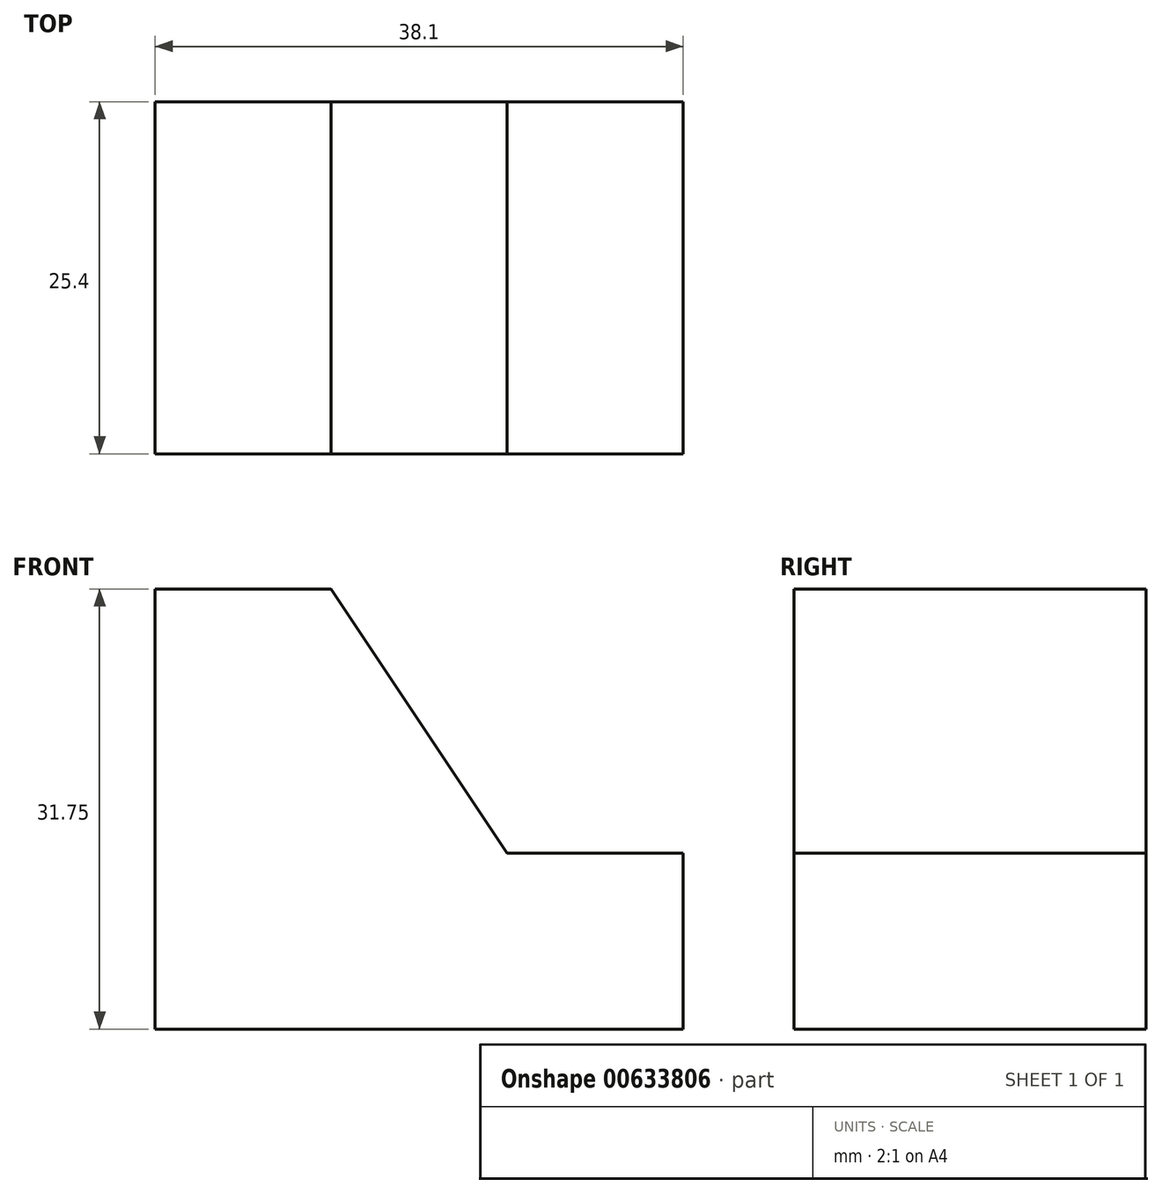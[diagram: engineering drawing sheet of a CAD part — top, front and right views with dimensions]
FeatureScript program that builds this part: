
annotation { "Feature Type Name" : "Feature", "Feature Type Description" : "" }
export const myFeature = defineFeature(function(context is Context, id is Id, definition is map)
    precondition{}
    {
        {
            var Q0;
            Q0=qCreatedBy(makeId("Front.planeOp"),FACE);
            var sketch = newSketch(context, id + "F0", { "sketchPlane" : qUnion([Q0])});
            skLineSegment(sketch, "E0", {"start": v(0, 0) * mm, "end": v(0, 31.75) * mm});
            skLineSegment(sketch, "E1", {"start": v(0, 0) * mm, "end": v(38.1, 0) * mm});
            skLineSegment(sketch, "E2", {"start": v(38.1, 0) * mm, "end": v(38.1, 12.7) * mm});
            skLineSegment(sketch, "E3", {"start": v(25.4, 12.7) * mm, "end": v(38.1, 12.7) * mm});
            skLineSegment(sketch, "E4", {"start": v(0, 31.75) * mm, "end": v(12.7, 31.75) * mm});
            skLineSegment(sketch, "E5", {"start": v(12.7, 31.75) * mm, "end": v(25.4, 12.7) * mm});
            skSolve(sketch);
        }
        {
            var Q0;
            Q0=makeQuery(id+"F0.imprint","IMPRINT",FACE,{"disambiguationData":[TD([[makeQuery(id+"F0.imprint","IMPRINT",EDGE,{"derivedFrom":sQuery(id+"F0.wireOp",EDGE,"E0")}),-1.0]])]});
            extrude(context, id + "F1", {"entities" : qUnion([Q0]), "depth" : 25.4 * mm, "offsetDistance" : 25.4 * mm});
        }
    });
